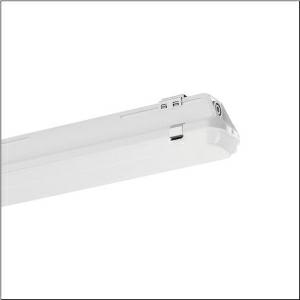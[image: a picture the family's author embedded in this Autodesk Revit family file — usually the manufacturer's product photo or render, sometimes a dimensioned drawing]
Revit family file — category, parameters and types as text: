
# Revit family: monsun_r__12_emergency_51fp207p467h3g_2c0c
name_source: partatom
category: Lighting Fixtures
units: mm (PartAtom-declared; Revit-internal decimal feet)

## family parameters
Cut with Voids When Loaded = No
Host = Face
Light Source = No
Part Type = Normal
Room Calculation Point = No
Round Connector Dimension = Use Diameter
Shared = No

## types (1)
- Monsun® 12 emergency (1 x LED, 5450 lm, 37.2 W, 4000K)
    Apparent Load = 37 VA
    CIE Flux Codes = 45 75 93 94 100
    Color Rendering = 80
    Color Temperature = 4000K
    Default Elevation = 1800 mm
    Description = Monsun® 12 emergency, damp-proof luminaire, chain hanger, primary optical cover: enclosure, of PC, light emission: direct distribution, primary light characteristic: symmetric, installation type: suspended mounting, surface-mounted, horizontal mounting, vertical mounting, LED rated luminous flux: 5.450 lm, light colour: 840, colour temperature: 4000K, control gear: ECG, with terminal, 4-pole, max. 2.5mm², mains connection: 220..240V, AC, 50/60Hz, rated input power: 37W, control gear: single battery element, battery: NiCd, 4,5 Ah, mains connection: 230V, luminaire housing, of glass-fibre reinforced polyester, uncoated, bright grey, length: 1.590 mm, width: 90 mm, height: 88mm, clip for enclosure, of stainless steel (V2A), ceiling mounting element, of stainless steel (V2A), chain hanger, of stainless steel (V2A), protection rating (complete): IP66, insulation class (complete): insulation class I (protective earthing), certification: CE, protection symbol: D, impact resistance: IK08, permissible ambient temperature for indoor applications: +5..+35°C, standard: EN 50419, EN 60598-2-1, EN 60598-2-22, no direct snow, no direct sun, no direct rain, for indoor or canopied outdoor use, corresponds to IFS (International Featured Standards) requirements for safety and quality in the food industry, packaging unit: 1 piece
    Height = 89 mm
    Lamp = 1 x LED
    Lamp Light Flux = 5450 lm
    Lamp Power = 37.2 W
    Lamp count = 1
    Length = 1590 mm
    Luminous efficacy = 147 lm/W
    Manufacturer = Siteco
    ModVariant = No
    Model = 51FP207P467H3G
    Mounting Place = Ceiling
    Mounting Type = Pendant
    Number of Poles = 1
    OnlyDefault = Yes
    Power Factor = 1
    Product Name = Monsun® 12 emergency
    Product group = damp-proof luminaire | ceiling pendant
    ProductGroupID = 908
    Protection Class = Protection class I
    Protection Degree = IP 66
    RLX_Detail_Level = 1
    RlxData = <blob elided: 88761 chars, md5=494d7cbf>
    Socket = socket
    Standby Power = 0 W
    System Light Flux = 5450 lm
    System Power = 37 W
    Type Comments = Product without accessories
    Type Image = l_1004748.jpg
    URL = http://relux.com
    VarID = ---
    Voltage = 0 V
    Weight = 0.00 kg
    Width = 90 mm

## geometry (parser evidence)
native form markers: Blend x4, Sweep x14
no freeform markers — native parametric forms only
